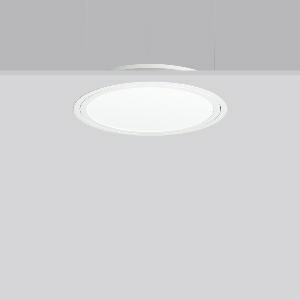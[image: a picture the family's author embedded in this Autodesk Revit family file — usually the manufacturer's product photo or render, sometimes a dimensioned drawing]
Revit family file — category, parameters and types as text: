
# Revit family: triona_round_e_312419_002_1_12_6d48
name_source: partatom
category: Lighting Fixtures
units: mm (PartAtom-declared; Revit-internal decimal feet)

## family parameters
Cut with Voids When Loaded = No
Host = Face
Light Source = No
Part Type = Normal
Room Calculation Point = No
Round Connector Dimension = Use Diameter
Shared = No

## types (1)
- TRIONA round E (1 x LED Modul 840, 4900 lm, 4000)
    Apparent Load = 48 VA
    CIE Flux Codes = 49 80 96 100 100
    Color Rendering = 80
    Color Temperature = 4000
    Default Elevation = 1800 mm
    Description = Series: TRIONA round
Decorative round LED recessed surface luminaire. Cover made of sheet steel, powder-coated. Frame made of aluminium, powder-coated. Recessed ring: aluminium extrusion profile, powder coated. Light emission through a diffuser: plastic, opal. Lightguide and diffuser made of non-yellowing plastic (PMMA). Lateral light emission (RZB SIDELITE technology) for above-average homogeneous light distribution. Suitable for installation in cavity ceilings. Tool-free mounting system thanks to the rocker arm mechanism (patent pending). Electronic ballast included. Very easy installation thanks to Plug+Play connection. 
Colour: traffic white, matt (RAL 9016)
Diameter: 505 mm
Height: 2 mm
Cut-out diameter: 482 mm
Recess height: 100 mm
Luminaire: recess height: 89 mm
Lamp: LED
Socket: without socket
Colour temperature: 4000K
Colour rendering index (CRI): 80
System power: 48 W
Rated luminous flux: 4900 lm
Luminous efficiency: 102 lm/W
Control gear: Converter, dimmable, DALI
Protection class: I
Type of protection: IP 40
    Height = 0 mm  [stored 0 ft]
    Lamp = 1 x LED Modul 840
    Lamp Light Flux = 4900 lm
    Lamp count = 1
    Length = 505 mm
    Lifetime = 50000 h
    Luminous efficacy = 102 lm/W
    Manufacturer = RZB
    ModVariant = No
    Model = 312419.002.1.12
    Mounting Place = Ceiling
    Mounting Type = Recessed
    Number of Poles = 1
    OnlyDefault = Yes
    Power Factor = 1
    Product Name = TRIONA round E
    Product group = Recessed modular luminaires
    ProductGroupID = 406
    Protection Class = Protection class I
    Protection Degree = IP 20
    RLX_Detail_Level = 1
    RLX_Emergency_Light_Flux = 0 lm
    RLX_Emergency_Type = 0
    RLX_Emergency_Type_DB = No
    RlxData = <blob elided: 30205 chars, md5=843116c0>
    Socket = socket
    Standby Power = 0 W
    System Light Flux = 4900 lm
    System Power = 48 W
    Type Comments = Product without accessories
    Type Image = 312419.002.12.jpg
    URL = http://relux.com
    VarID = ---
    Voltage = 230 V
    Voltage Range = 220-240 V
    Weight = 0.00 kg
    Width = 0 mm  [stored 0 ft]

note: [stored X ft] marks values corroborated as IEEE doubles in the binary element streams (Revit-internal decimal feet)

## geometry (parser evidence)
native form markers: Blend x4, Sweep x11
no freeform markers — native parametric forms only
